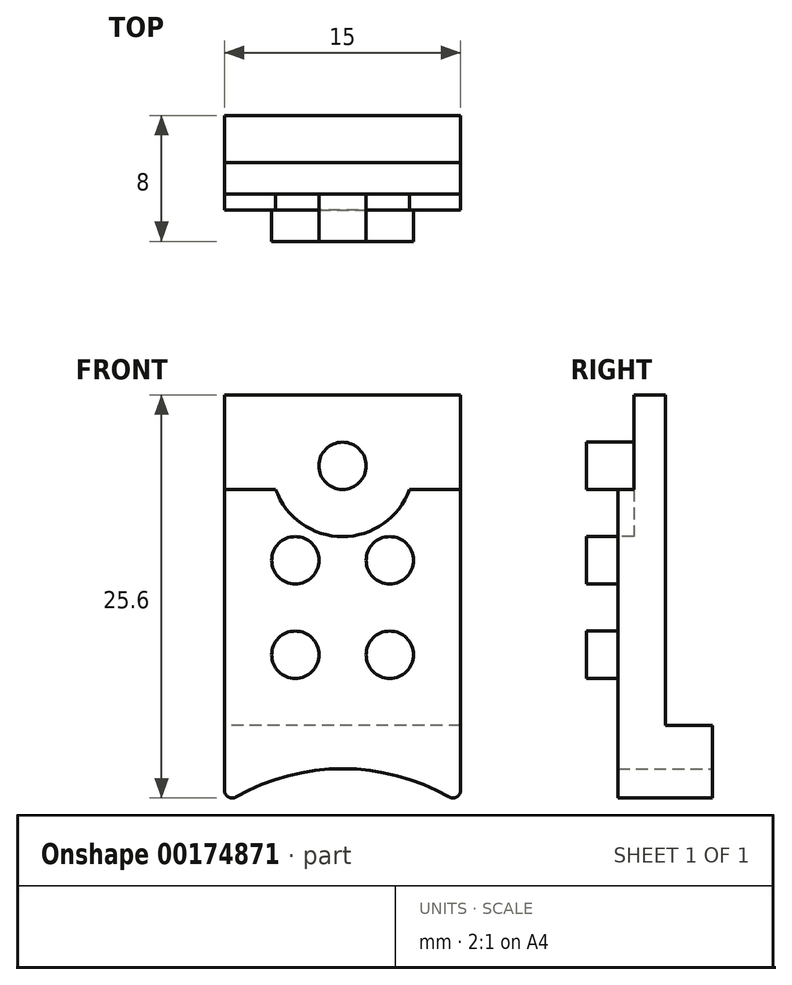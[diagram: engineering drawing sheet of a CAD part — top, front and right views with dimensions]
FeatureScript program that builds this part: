
annotation { "Feature Type Name" : "Feature", "Feature Type Description" : "" }
export const myFeature = defineFeature(function(context is Context, id is Id, definition is map)
    precondition{}
    {
        {
            var Q0;
            Q0=qCreatedBy(makeId("Front.planeOp"),FACE);
            var sketch = newSketch(context, id + "F0", { "sketchPlane" : qUnion([Q0])});
            skLineSegment(sketch, "E0.bottom", {"start": v(7.5, 7.5) * mm, "end": v(-7.5, 7.5) * mm});
            skLineSegment(sketch, "E0.top", {"start": v(7.5, -7.5) * mm, "end": v(-7.5, -7.5) * mm});
            skLineSegment(sketch, "E0.left", {"start": v(7.5, 7.5) * mm, "end": v(7.5, -7.5) * mm});
            skLineSegment(sketch, "E0.right", {"start": v(-7.5, 7.5) * mm, "end": v(-7.5, -7.5) * mm});
            skPoint(sketch, "E0.middle", {"position": v(0, 0) * mm});
            skLineSegment(sketch, "E1.bottom", {"start": v(-7.5, 7.5) * mm, "end": v(7.5, 7.5) * mm});
            skLineSegment(sketch, "E1.top", {"start": v(-7.5, 13.5) * mm, "end": v(7.5, 13.5) * mm});
            skLineSegment(sketch, "E1.left", {"start": v(-7.5, 7.5) * mm, "end": v(-7.5, 13.5) * mm});
            skLineSegment(sketch, "E1.right", {"start": v(7.5, 7.5) * mm, "end": v(7.5, 13.5) * mm});
            skSolve(sketch);
        }
        {
            var Q0;
            Q0 = qSketchRegion(id + "F0", true);
            extrude(context, id + "F1", {"entities" : qUnion([Q0]), "depth" : 10 * mm});
        }
        {
            var Q0;
            Q0=makeQuery(id+"F1.opExtrude","CAP_FACE",FACE,{"disambiguationData":[OSD([sQuery(id+"F0.wireOp",EDGE,"E0.top"),sQuery(id+"F0.wireOp",EDGE,"E0.left"),sQuery(id+"F0.wireOp",EDGE,"E0.right"),sQuery(id+"F0.wireOp",EDGE,"E1.top"),sQuery(id+"F0.wireOp",EDGE,"E1.left"),sQuery(id+"F0.wireOp",EDGE,"E1.right")])],"isStart":false});
            var sketch = newSketch(context, id + "F2", { "sketchPlane" : qUnion([Q0])});
            skCircle(sketch, "E2", {"center": v(-3, 3) * mm, "radius": 1.5 * mm});
            skCircle(sketch, "E3", {"center": v(-3, -3) * mm, "radius": 1.5 * mm});
            skCircle(sketch, "E4", {"center": v(3, -3) * mm, "radius": 1.5 * mm});
            skCircle(sketch, "E5", {"center": v(3, 3) * mm, "radius": 1.5 * mm});
            skSolve(sketch);
        }
        {
            var Q0;
            Q0 = qSketchRegion(id + "F2", true);
            extrude(context, id + "F3", {"entities" : qUnion([Q0]), "operationType" : NewBodyOperationType.ADD, "depth" : 2 * mm});
        }
        {
            var Q0;
            Q0=makeQuery(id+"F1.opExtrude","CAP_FACE",FACE,{"disambiguationData":[OSD([sQuery(id+"F0.wireOp",EDGE,"E0.top"),sQuery(id+"F0.wireOp",EDGE,"E0.left"),sQuery(id+"F0.wireOp",EDGE,"E0.right"),sQuery(id+"F0.wireOp",EDGE,"E1.top"),sQuery(id+"F0.wireOp",EDGE,"E1.left"),sQuery(id+"F0.wireOp",EDGE,"E1.right")])],"isStart":false});
            var sketch = newSketch(context, id + "F4", { "sketchPlane" : qUnion([Q0])});
            skLineSegment(sketch, "E6", {"start": v(-7.5, 7.5) * mm, "end": v(7.5, 7.5) * mm});
            skCircle(sketch, "E7", {"center": v(0, 9) * mm, "radius": 1.5 * mm});
            skCircle(sketch, "E8", {"center": v(0, 9) * mm, "radius": 4.5 * mm});
            skLineSegment(sketch, "E9", {"start": v(-7.5, 7.5) * mm, "end": v(-7.5, 13.5) * mm});
            skLineSegment(sketch, "E10", {"start": v(-7.5, 13.5) * mm, "end": v(7.5, 13.5) * mm});
            skLineSegment(sketch, "E11", {"start": v(7.5, 13.5) * mm, "end": v(7.5, 7.5) * mm});
            skSolve(sketch);
        }
        {
            var Q0;
            Q0 = qSketchRegion(id + "F4", true);
            extrude(context, id + "F5", {"entities" : qUnion([Q0]), "operationType" : NewBodyOperationType.REMOVE, "oppositeDirection" : true, "depth" : 1 * mm});
        }
        {
            var Q0;
            Q0=makeQuery(id+"F5.boolean.opBoolean","SPLIT",FACE,{"disambiguationData":[TD([makeQuery(id+"F5.opExtrude","SWEPT_FACE",FACE,{"disambiguationData":[OSD([sQuery(id+"F4.wireOp",EDGE,"E7")])]})])],"derivedFrom":makeQuery(id+"F1.opExtrude","CAP_FACE",FACE,{"disambiguationData":[OSD([sQuery(id+"F0.wireOp",EDGE,"E0.top"),sQuery(id+"F0.wireOp",EDGE,"E0.left"),sQuery(id+"F0.wireOp",EDGE,"E0.right"),sQuery(id+"F0.wireOp",EDGE,"E1.top"),sQuery(id+"F0.wireOp",EDGE,"E1.left"),sQuery(id+"F0.wireOp",EDGE,"E1.right")])],"isStart":false})});
            var sketch = newSketch(context, id + "F6", { "sketchPlane" : qUnion([Q0])});
            skCircle(sketch, "E12", {"center": v(0, 9) * mm, "radius": 1.5 * mm});
            skSolve(sketch);
        }
        {
            var Q0;
            Q0 = qSketchRegion(id + "F6", true);
            extrude(context, id + "F7", {"entities" : qUnion([Q0]), "operationType" : NewBodyOperationType.ADD, "depth" : 2 * mm});
        }
        {
            var Q0;
            Q0=makeQuery(id+"F1.opExtrude","CAP_FACE",FACE,{"disambiguationData":[OSD([sQuery(id+"F0.wireOp",EDGE,"E0.top"),sQuery(id+"F0.wireOp",EDGE,"E0.left"),sQuery(id+"F0.wireOp",EDGE,"E0.right"),sQuery(id+"F0.wireOp",EDGE,"E1.top"),sQuery(id+"F0.wireOp",EDGE,"E1.left"),sQuery(id+"F0.wireOp",EDGE,"E1.right")])],"isStart":true});
            var sketch = newSketch(context, id + "F8", { "sketchPlane" : qUnion([Q0])});
            skLineSegment(sketch, "E13.bottom", {"start": v(-7.5, 13.5) * mm, "end": v(7.5, 13.5) * mm});
            skLineSegment(sketch, "E13.top", {"start": v(-7.5, -7.5) * mm, "end": v(7.5, -7.5) * mm});
            skLineSegment(sketch, "E13.left", {"start": v(-7.5, 13.5) * mm, "end": v(-7.5, -7.5) * mm});
            skLineSegment(sketch, "E13.right", {"start": v(7.5, 13.5) * mm, "end": v(7.5, -7.5) * mm});
            skSolve(sketch);
        }
        {
            var Q0;
            Q0 = qSketchRegion(id + "F8", true);
            extrude(context, id + "F9", {"entities" : qUnion([Q0]), "operationType" : NewBodyOperationType.REMOVE, "oppositeDirection" : true, "depth" : 7 * mm});
        }
        {
            var Q0;
            Q0=makeQuery(id+"F1.opExtrude","SWEPT_FACE",FACE,{"disambiguationData":[OSD([sQuery(id+"F0.wireOp",EDGE,"E0.top")])]});
            var sketch = newSketch(context, id + "F10", { "sketchPlane" : qUnion([Q0])});
            skLineSegment(sketch, "E14.bottom", {"start": v(7.5, 7) * mm, "end": v(-7.5, 7) * mm});
            skLineSegment(sketch, "E14.top", {"start": v(7.5, 10) * mm, "end": v(-7.5, 10) * mm});
            skLineSegment(sketch, "E14.left", {"start": v(7.5, 7) * mm, "end": v(7.5, 10) * mm});
            skLineSegment(sketch, "E14.right", {"start": v(-7.5, 7) * mm, "end": v(-7.5, 10) * mm});
            skSolve(sketch);
        }
        {
            var Q0;
            Q0 = qSketchRegion(id + "F10", true);
            extrude(context, id + "F11", {"entities" : qUnion([Q0]), "operationType" : NewBodyOperationType.ADD, "depth" : 5 * mm});
        }
        {
            var Q0;
            Q0=makeQuery(id+"F11.boolean.opBoolean","MERGE",FACE,{"derivedFrom":[makeQuery(id+"F9.boolean.opBoolean","COPY",FACE,{"derivedFrom":makeQuery(id+"F9.opExtrude","CAP_FACE",FACE,{"disambiguationData":[OSD([sQuery(id+"F8.wireOp",EDGE,"E13.bottom"),sQuery(id+"F8.wireOp",EDGE,"E13.top"),sQuery(id+"F8.wireOp",EDGE,"E13.left"),sQuery(id+"F8.wireOp",EDGE,"E13.right")])],"isStart":false})}),makeQuery(id+"F11.opExtrude","SWEPT_FACE",FACE,{"disambiguationData":[OSD([sQuery(id+"F10.wireOp",EDGE,"E14.bottom")])]})]});
            var sketch = newSketch(context, id + "F12", { "sketchPlane" : qUnion([Q0])});
            skLineSegment(sketch, "E15.bottom", {"start": v(-7.5, -12.5) * mm, "end": v(7.5, -12.5) * mm});
            skLineSegment(sketch, "E15.top", {"start": v(-7.5, -7.5) * mm, "end": v(7.5, -7.5) * mm});
            skLineSegment(sketch, "E15.left", {"start": v(-7.5, -12.5) * mm, "end": v(-7.5, -7.5) * mm});
            skLineSegment(sketch, "E15.right", {"start": v(7.5, -12.5) * mm, "end": v(7.5, -7.5) * mm});
            skSolve(sketch);
        }
        {
            var Q0;
            Q0 = qSketchRegion(id + "F12", true);
            extrude(context, id + "F13", {"entities" : qUnion([Q0]), "operationType" : NewBodyOperationType.ADD, "depth" : 3 * mm});
        }
        {
            var Q0;
            Q0=makeQuery(id+"F13.opExtrude","CAP_FACE",FACE,{"disambiguationData":[OSD([sQuery(id+"F12.wireOp",EDGE,"E15.bottom"),sQuery(id+"F12.wireOp",EDGE,"E15.top"),sQuery(id+"F12.wireOp",EDGE,"E15.left"),sQuery(id+"F12.wireOp",EDGE,"E15.right")])],"isStart":false});
            var sketch = newSketch(context, id + "F14", { "sketchPlane" : qUnion([Q0])});
            skArc(sketch, "E16", {"start": v(7.5, -12.5) * mm, "mid": v(0, -10.24) * mm, "end": v(-7.5, -12.5) * mm});
            skLineSegment(sketch, "E17", {"start": v(-7.5, -12.5) * mm, "end": v(7.5, -12.5) * mm});
            skSolve(sketch);
        }
        {
            var Q0;
            Q0 = qSketchRegion(id + "F14", true);
            extrude(context, id + "F15", {"entities" : qUnion([Q0]), "operationType" : NewBodyOperationType.REMOVE, "oppositeDirection" : true, "depth" : 25 * mm});
        }
        {
            var Q0;
            {var subQ0=sQuery(id+"F12.wireOp",EDGE,"E15.right");Q0=makeQuery(id+"F15.boolean.opBoolean","MERGE",EDGE,{"derivedFrom":[makeQuery(id+"F13.boolean.opBoolean","MERGE",EDGE,{"derivedFrom":[makeQuery(id+"F11.opExtrude","CAP_EDGE",EDGE,{"disambiguationData":[OSD([sQuery(id+"F10.wireOp",EDGE,"E14.right")])],"isStart":false}),makeQuery(id+"F13.opExtrude","SWEPT_EDGE",EDGE,{"disambiguationData":[OSD([sQuery(id+"F12.wireOp",EDGE,"E15.bottom"),subQ0])]})]}),makeQuery(id+"F15.opExtrude","SWEPT_EDGE",EDGE,{"disambiguationData":[OSD([subQ0,sQuery(id+"F14.wireOp",EDGE,"E16"),sQuery(id+"F14.wireOp",EDGE,"E17")])]})]});}
            var Q1;
            {var subQ0=sQuery(id+"F12.wireOp",EDGE,"E15.left");Q1=makeQuery(id+"F15.boolean.opBoolean","MERGE",EDGE,{"derivedFrom":[makeQuery(id+"F13.boolean.opBoolean","MERGE",EDGE,{"derivedFrom":[makeQuery(id+"F11.opExtrude","CAP_EDGE",EDGE,{"disambiguationData":[OSD([sQuery(id+"F10.wireOp",EDGE,"E14.left")])],"isStart":false}),makeQuery(id+"F13.opExtrude","SWEPT_EDGE",EDGE,{"disambiguationData":[OSD([sQuery(id+"F12.wireOp",EDGE,"E15.bottom"),subQ0])]})]}),makeQuery(id+"F15.opExtrude","SWEPT_EDGE",EDGE,{"disambiguationData":[OSD([subQ0,sQuery(id+"F14.wireOp",EDGE,"E16"),sQuery(id+"F14.wireOp",EDGE,"E17")])]})]});}
            fillet(context, id + "F16", {"entities" : qUnion([Q0, Q1]), "radius" : .5 * mm, "tangentPropagation" : true, "allowEdgeOverflow" : false});
        }
    });
